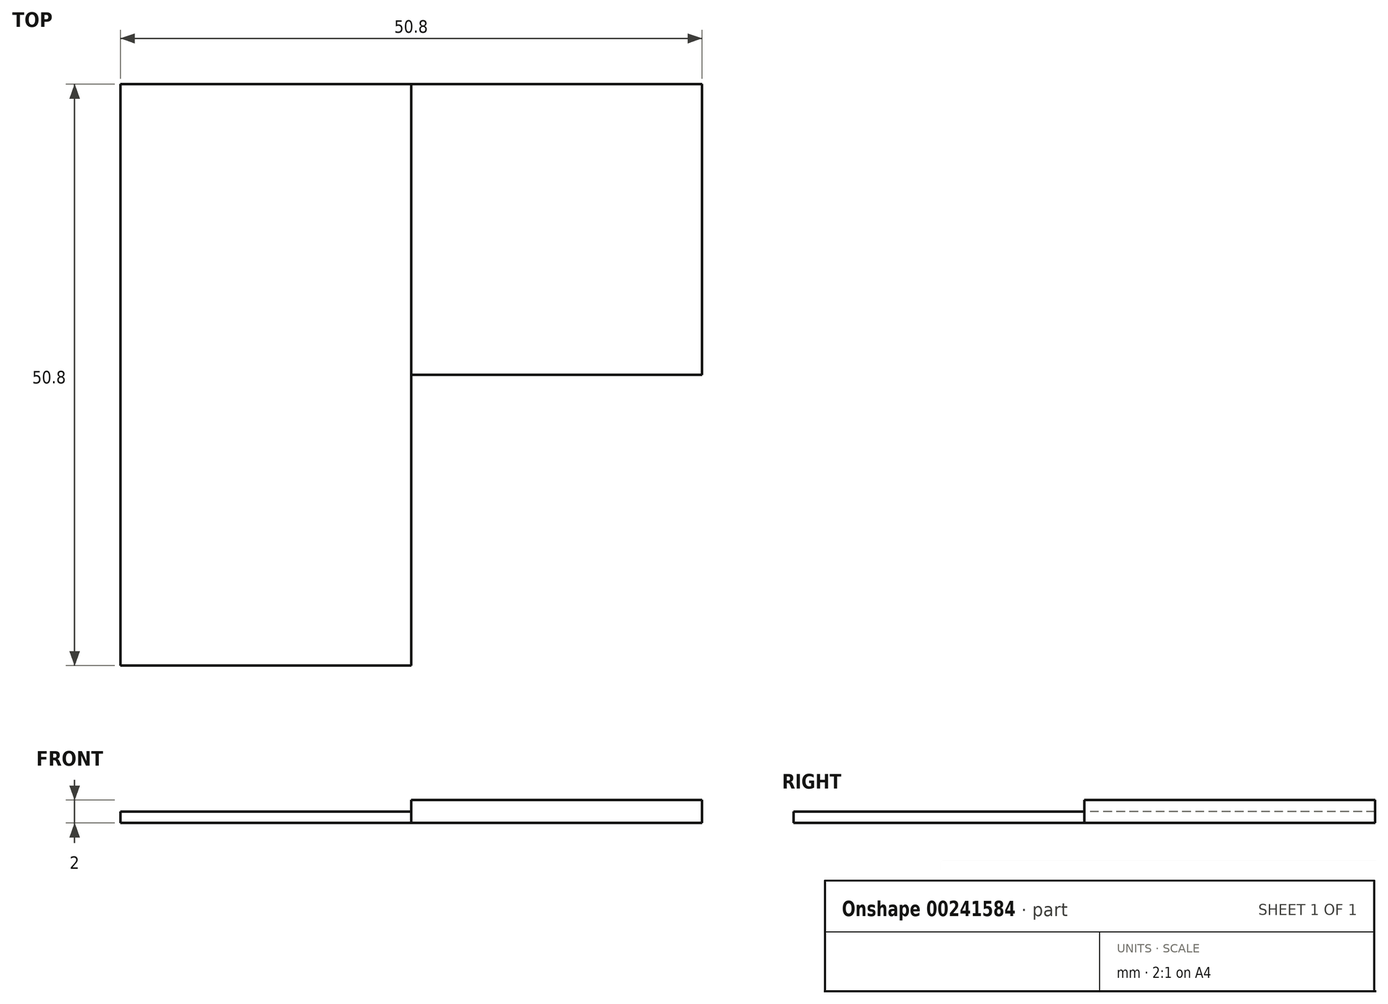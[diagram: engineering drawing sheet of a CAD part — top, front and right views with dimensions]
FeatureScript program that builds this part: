
annotation { "Feature Type Name" : "Feature", "Feature Type Description" : "" }
export const myFeature = defineFeature(function(context is Context, id is Id, definition is map)
    precondition{}
    {
        {
            assignVariable(context, id + "F0", {"name" : "x", "anyValue" : 1});
        }
        {
            var Q0;
            Q0=qCreatedBy(makeId("Top.planeOp"),FACE);
            var sketch = newSketch(context, id + "F1", { "sketchPlane" : qUnion([Q0])});
            skLineSegment(sketch, "E0.bottom", {"start": v(25.4, 25.4) * mm, "end": v(-25.4, 25.4) * mm});
            skLineSegment(sketch, "E0.top", {"start": v(25.4, -25.4) * mm, "end": v(-25.4, -25.4) * mm});
            skLineSegment(sketch, "E0.left", {"start": v(25.4, 25.4) * mm, "end": v(25.4, -25.4) * mm});
            skLineSegment(sketch, "E0.right", {"start": v(-25.4, 25.4) * mm, "end": v(-25.4, -25.4) * mm});
            skPoint(sketch, "E0.middle", {"position": v(0, 0) * mm});
            skSolve(sketch);
        }
        {
            var Q0;
            Q0=makeQuery(id+"F1.imprint","IMPRINT",FACE,{"disambiguationData":[TD([[makeQuery(id+"F1.imprint","IMPRINT",EDGE,{"derivedFrom":sQuery(id+"F1.wireOp",EDGE,"E0.bottom")}),1.0]])]});
            extrude(context, id + "F2", {"entities" : qUnion([Q0]), "depth" : (getVariable(context, 'x')) * mm});
        }
        {
            var Q0;
            Q0=makeQuery(id+"F2.opExtrude","CAP_FACE",FACE,{"disambiguationData":[OSD([sQuery(id+"F1.wireOp",EDGE,"E0.bottom"),sQuery(id+"F1.wireOp",EDGE,"E0.top"),sQuery(id+"F1.wireOp",EDGE,"E0.left"),sQuery(id+"F1.wireOp",EDGE,"E0.right")])],"isStart":false});
            var sketch = newSketch(context, id + "F3", { "sketchPlane" : qUnion([Q0])});
            skLineSegment(sketch, "E1.bottom", {"start": v(25.4, -25.4) * mm, "end": v(0, -25.4) * mm});
            skLineSegment(sketch, "E1.top", {"start": v(25.4, 0) * mm, "end": v(0, 0) * mm});
            skLineSegment(sketch, "E1.left", {"start": v(25.4, -25.4) * mm, "end": v(25.4, 0) * mm});
            skLineSegment(sketch, "E1.right", {"start": v(0, -25.4) * mm, "end": v(0, 0) * mm});
            skSolve(sketch);
        }
        {
            var Q0;
            Q0=makeQuery(id+"F3.imprint","IMPRINT",FACE,{"disambiguationData":[TD([[makeQuery(id+"F3.imprint","IMPRINT",EDGE,{"derivedFrom":sQuery(id+"F3.wireOp",EDGE,"E1.bottom")}),-1.0]])]});
            extrude(context, id + "F4", {"entities" : qUnion([Q0]), "operationType" : NewBodyOperationType.REMOVE, "oppositeDirection" : true, "depth" : (getVariable(context, 'x')) * mm});
        }
        {
            var Q0;
            Q0=makeQuery(id+"F2.opExtrude","CAP_FACE",FACE,{"disambiguationData":[OSD([sQuery(id+"F1.wireOp",EDGE,"E0.bottom"),sQuery(id+"F1.wireOp",EDGE,"E0.top"),sQuery(id+"F1.wireOp",EDGE,"E0.left"),sQuery(id+"F1.wireOp",EDGE,"E0.right")])],"isStart":false});
            var sketch = newSketch(context, id + "F5", { "sketchPlane" : qUnion([Q0])});
            skLineSegment(sketch, "E2.bottom", {"start": v(25.4, 25.4) * mm, "end": v(0, 25.4) * mm});
            skLineSegment(sketch, "E2.top", {"start": v(25.4, 0) * mm, "end": v(0, 0) * mm});
            skLineSegment(sketch, "E2.left", {"start": v(25.4, 25.4) * mm, "end": v(25.4, 0) * mm});
            skLineSegment(sketch, "E2.right", {"start": v(0, 25.4) * mm, "end": v(0, 0) * mm});
            skSolve(sketch);
        }
        {
            var Q0;
            Q0=makeQuery(id+"F5.imprint","IMPRINT",FACE,{"disambiguationData":[TD([[makeQuery(id+"F5.imprint","IMPRINT",EDGE,{"derivedFrom":sQuery(id+"F5.wireOp",EDGE,"E2.bottom")}),1.0]])]});
            extrude(context, id + "F6", {"entities" : qUnion([Q0]), "operationType" : NewBodyOperationType.ADD, "depth" : (getVariable(context, 'x')) * mm});
        }
    });
